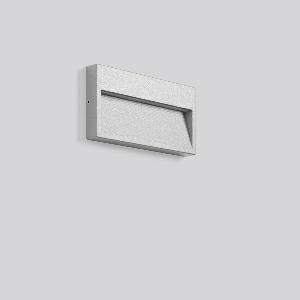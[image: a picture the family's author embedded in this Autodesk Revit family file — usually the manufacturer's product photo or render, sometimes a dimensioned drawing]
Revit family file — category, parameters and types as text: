
# Revit family: brick_duo_581634_004_1_3c87
name_source: partatom
category: Lighting Fixtures
units: mm (PartAtom-declared; Revit-internal decimal feet)

## family parameters
Cut with Voids When Loaded = No
Host = Face
Light Source = No
Part Type = Normal
Room Calculation Point = No
Round Connector Dimension = Use Diameter
Shared = No

## types (1)
- BRICK duo (1 x LED Modul 840, 180 lm, 4000)
    Apparent Load = 10 VA
    CIE Flux Codes = 49 80 95 96 100
    Color Rendering = 80
    Color Temperature = 4000
    Default Elevation = 1800 mm
    Description = Series: BRICK duo
Flat surface-mounted LED fitting for illumination of wall related areas such as stairs, ramps or corridors. Housing made of corrosion-resistant die-cast aluminium, powder-coated. Stainless steel screws. Diffuser with clear toughened glass. Asymmetrical downward light distribution for wide dispersion and uniform illumination. With compensation for drill hole deviations. Driver integrated. With connecting terminal up to 1 x 3 x 1.5 mm², for max. 13 mm diameter mains cable. 
Colour: silver, matt (approx. RAL 9006)
Length: 240 mm
Width: 120 mm
Height: 24 mm
Lamp: LED
System power: 10 W
Rated luminous flux: 180 lm
Luminous efficiency: 18 lm/W
Control gear: Regulated power supply
Protection class: I
Type of protection: IP 65
    Height = 24 mm  [stored 0.0787402 ft]
    Lamp = 1 x LED Modul 840
    Lamp Light Flux = 180 lm
    Lamp count = 1
    Length = 240 mm
    Lifetime = 50000 h
    Luminous efficacy = 18 lm/W
    Manufacturer = RZB
    ModVariant = No
    Model = 581634.004.1
    Mounting Place = Wall
    Mounting Type = Surface mounted
    Number of Poles = 1
    OnlyDefault = Yes
    Power Factor = 1
    Product Name = BRICK duo
    Product group = Surface mounted Wall luminaires
    ProductGroupID = 2001
    Protection Class = Protection class I
    Protection Degree = IP 65
    RLX_Detail_Level = 1
    RLX_Emergency_Light_Flux = 0 lm
    RLX_Emergency_Type = 0
    RLX_Emergency_Type_DB = No
    RlxData = <blob elided: 18877 chars, md5=d7f1ab0b>
    Socket = socket
    Standby Power = 0 W
    System Light Flux = 180 lm
    System Power = 10 W
    Type Comments = ALEA SPOT
    Type Image = 581634.004.jpg
    URL = http://relux.com
    VarID = ---
    Voltage = 0 V
    Weight = 0.00 kg
    Width = 120 mm

note: [stored X ft] marks values corroborated as IEEE doubles in the binary element streams (Revit-internal decimal feet)

## geometry (parser evidence)
native form markers: Blend x4, Sweep x12
no freeform markers — native parametric forms only
